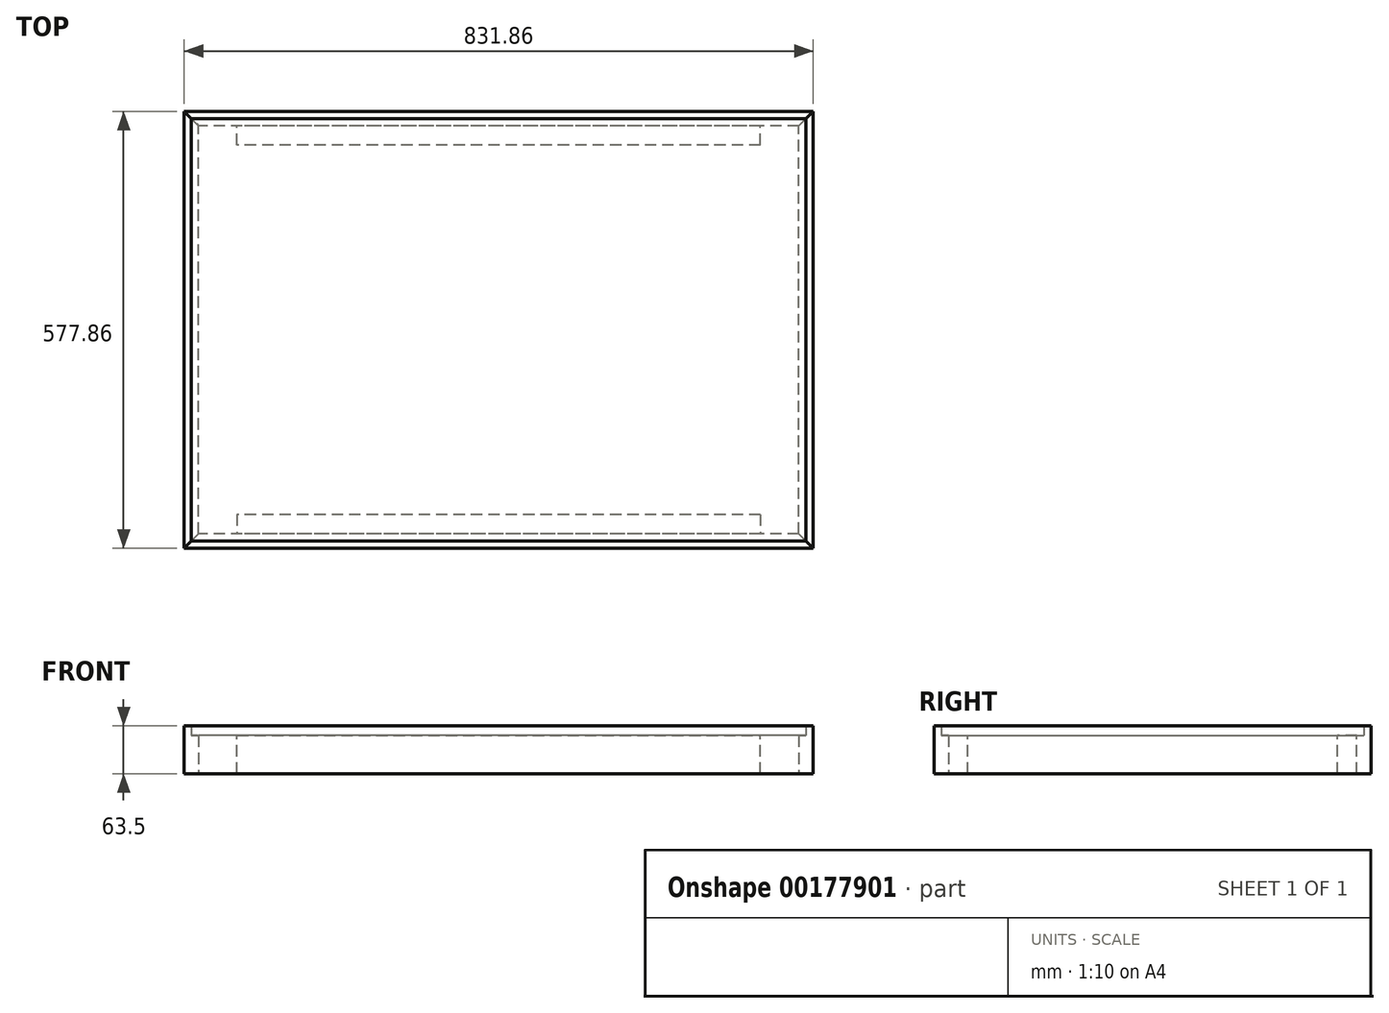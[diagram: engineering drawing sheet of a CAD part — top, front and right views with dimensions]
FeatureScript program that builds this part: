
annotation { "Feature Type Name" : "Feature", "Feature Type Description" : "" }
export const myFeature = defineFeature(function(context is Context, id is Id, definition is map)
    precondition{}
    {
        {
            var Q0;
            Q0=qCreatedBy(makeId("Top.planeOp"),FACE);
            var sketch = newSketch(context, id + "F0", { "sketchPlane" : qUnion([Q0])});
            skLineSegment(sketch, "E0.bottom", {"start": v(406.4, -279.4) * mm, "end": v(-406.4, -279.4) * mm});
            skLineSegment(sketch, "E0.top", {"start": v(406.4, 279.4) * mm, "end": v(-406.4, 279.4) * mm});
            skLineSegment(sketch, "E0.left", {"start": v(406.4, -279.4) * mm, "end": v(406.4, 279.4) * mm});
            skLineSegment(sketch, "E0.right", {"start": v(-406.4, -279.4) * mm, "end": v(-406.4, 279.4) * mm});
            skPoint(sketch, "E0.middle", {"position": v(0, 0) * mm});
            skLineSegment(sketch, "E1.0", {"start": v(-396.88, -269.87) * mm, "end": v(-396.88, 269.88) * mm});
            skLineSegment(sketch, "E1.1", {"start": v(396.88, -269.87) * mm, "end": v(-396.88, -269.87) * mm});
            skLineSegment(sketch, "E1.2", {"start": v(396.88, -269.87) * mm, "end": v(396.88, 269.88) * mm});
            skLineSegment(sketch, "E1.3", {"start": v(396.88, 269.88) * mm, "end": v(-396.88, 269.88) * mm});
            skLineSegment(sketch, "E2.0", {"start": v(-415.93, -288.92) * mm, "end": v(-415.93, 288.93) * mm});
            skLineSegment(sketch, "E2.1", {"start": v(415.93, -288.92) * mm, "end": v(-415.93, -288.92) * mm});
            skLineSegment(sketch, "E2.2", {"start": v(415.93, -288.92) * mm, "end": v(415.93, 288.93) * mm});
            skLineSegment(sketch, "E2.3", {"start": v(415.93, 288.93) * mm, "end": v(-415.93, 288.93) * mm});
            skLineSegment(sketch, "E3", {"start": v(-415.93, 288.93) * mm, "end": v(-396.88, 269.88) * mm});
            skLineSegment(sketch, "E4", {"start": v(-415.93, -288.92) * mm, "end": v(-396.88, -269.87) * mm});
            skLineSegment(sketch, "E5", {"start": v(396.88, -269.87) * mm, "end": v(415.93, -288.92) * mm});
            skLineSegment(sketch, "E6", {"start": v(396.88, 269.88) * mm, "end": v(415.93, 288.93) * mm});
            skSolve(sketch);
        }
        {
            var Q0;
            Q0=makeQuery(id+"F0.imprint","IMPRINT",FACE,{"disambiguationData":[TD([[makeQuery(id+"F0.imprint","IMPRINT",EDGE,{"derivedFrom":sQuery(id+"F0.wireOp",EDGE,"E0.bottom")}),-1.0]])]});
            var Q1;
            Q1=makeQuery(id+"F0.imprint","IMPRINT",FACE,{"disambiguationData":[TD([[makeQuery(id+"F0.imprint","IMPRINT",EDGE,{"derivedFrom":sQuery(id+"F0.wireOp",EDGE,"E1.0")}),-1.0]])]});
            var Q2;
            {var subQ0=sQuery(id+"F0.wireOp",EDGE,"E0.right");Q2=makeQuery(id+"F0.imprint","IMPRINT",FACE,{"disambiguationData":[TD([[makeQuery(id+"F0.imprint","IMPRINT",EDGE,{"derivedFrom":subQ0}),-1.0]])]});}
            var Q3;
            {var subQ0=sQuery(id+"F0.wireOp",EDGE,"E0.top");Q3=makeQuery(id+"F0.imprint","IMPRINT",FACE,{"disambiguationData":[TD([[makeQuery(id+"F0.imprint","IMPRINT",EDGE,{"derivedFrom":subQ0}),1.0]])]});}
            var Q4;
            {var subQ0=sQuery(id+"F0.wireOp",EDGE,"E0.left");Q4=makeQuery(id+"F0.imprint","IMPRINT",FACE,{"disambiguationData":[TD([[makeQuery(id+"F0.imprint","IMPRINT",EDGE,{"derivedFrom":subQ0}),1.0]])]});}
            extrude(context, id + "F1", {"entities" : qUnion([Q0, Q1, Q2, Q3, Q4]), "depth" : 12.7 * mm});
        }
        {
            var Q0;
            {var subQ0=sQuery(id+"F0.wireOp",EDGE,"E0.right");Q0=makeQuery(id+"F0.imprint","IMPRINT",FACE,{"disambiguationData":[TD([[makeQuery(id+"F0.imprint","IMPRINT",EDGE,{"derivedFrom":subQ0}),-1.0]])]});}
            var Q1;
            {var subQ0=sQuery(id+"F0.wireOp",EDGE,"E0.right");Q1=makeQuery(id+"F0.imprint","IMPRINT",FACE,{"disambiguationData":[TD([[makeQuery(id+"F0.imprint","IMPRINT",EDGE,{"derivedFrom":subQ0}),1.0]])]});}
            var Q2;
            Q2=makeQuery(id+"F1.opExtrude","CAP_FACE",FACE,{"disambiguationData":[OSD([sQuery(id+"F0.wireOp",EDGE,"E0.bottom"),sQuery(id+"F0.wireOp",EDGE,"E0.top"),sQuery(id+"F0.wireOp",EDGE,"E0.left"),sQuery(id+"F0.wireOp",EDGE,"E0.right")])],"isStart":false});
            extrude(context, id + "F2", {"entities" : qUnion([Q0, Q1]), "endBound" : BoundingType.UP_TO_SURFACE, "endBoundEntityFace" : qUnion([Q2]), "depth" : 25.4 * mm, "hasSecondDirection" : true, "secondDirectionOppositeDirection" : true, "secondDirectionDepth" : 50.8 * mm});
        }
        {
            var Q0;
            {var subQ0=sQuery(id+"F0.wireOp",EDGE,"E0.bottom");Q0=makeQuery(id+"F0.imprint","IMPRINT",FACE,{"disambiguationData":[TD([[makeQuery(id+"F0.imprint","IMPRINT",EDGE,{"derivedFrom":subQ0}),-1.0]])]});}
            var Q1;
            {var subQ0=sQuery(id+"F0.wireOp",EDGE,"E0.bottom");Q1=makeQuery(id+"F0.imprint","IMPRINT",FACE,{"disambiguationData":[TD([[makeQuery(id+"F0.imprint","IMPRINT",EDGE,{"derivedFrom":subQ0}),1.0]])]});}
            var Q2;
            Q2=makeQuery(id+"F1.opExtrude","CAP_FACE",FACE,{"disambiguationData":[OSD([sQuery(id+"F0.wireOp",EDGE,"E0.bottom"),sQuery(id+"F0.wireOp",EDGE,"E0.top"),sQuery(id+"F0.wireOp",EDGE,"E0.left"),sQuery(id+"F0.wireOp",EDGE,"E0.right")])],"isStart":false});
            var Q3;
            Q3=makeQuery(id+"F2.opExtrude","CAP_FACE",FACE,{"disambiguationData":[OSD([sQuery(id+"F0.wireOp",EDGE,"E1.0"),sQuery(id+"F0.wireOp",EDGE,"E2.0"),sQuery(id+"F0.wireOp",EDGE,"E3"),sQuery(id+"F0.wireOp",EDGE,"E4")])],"isStart":true});
            extrude(context, id + "F3", {"entities" : qUnion([Q0, Q1]), "endBound" : BoundingType.UP_TO_SURFACE, "endBoundEntityFace" : qUnion([Q2]), "depth" : 25.4 * mm, "hasSecondDirection" : true, "secondDirectionBound" : SecondDirectionBoundingType.UP_TO_SURFACE, "secondDirectionOppositeDirection" : true, "secondDirectionBoundEntityFace" : qUnion([Q3]), "secondDirectionDepth" : 25.4 * mm});
        }
        {
            var Q0;
            {var subQ0=sQuery(id+"F0.wireOp",EDGE,"E0.left");Q0=makeQuery(id+"F0.imprint","IMPRINT",FACE,{"disambiguationData":[TD([[makeQuery(id+"F0.imprint","IMPRINT",EDGE,{"derivedFrom":subQ0}),1.0]])]});}
            var Q1;
            {var subQ0=sQuery(id+"F0.wireOp",EDGE,"E0.left");Q1=makeQuery(id+"F0.imprint","IMPRINT",FACE,{"disambiguationData":[TD([[makeQuery(id+"F0.imprint","IMPRINT",EDGE,{"derivedFrom":subQ0}),-1.0]])]});}
            var Q2;
            Q2=makeQuery(id+"F1.opExtrude","CAP_FACE",FACE,{"disambiguationData":[OSD([sQuery(id+"F0.wireOp",EDGE,"E0.bottom"),sQuery(id+"F0.wireOp",EDGE,"E0.top"),sQuery(id+"F0.wireOp",EDGE,"E0.left"),sQuery(id+"F0.wireOp",EDGE,"E0.right")])],"isStart":false});
            var Q3;
            Q3=makeQuery(id+"F2.opExtrude","CAP_FACE",FACE,{"disambiguationData":[OSD([sQuery(id+"F0.wireOp",EDGE,"E1.0"),sQuery(id+"F0.wireOp",EDGE,"E2.0"),sQuery(id+"F0.wireOp",EDGE,"E3"),sQuery(id+"F0.wireOp",EDGE,"E4")])],"isStart":true});
            extrude(context, id + "F4", {"entities" : qUnion([Q0, Q1]), "endBound" : BoundingType.UP_TO_SURFACE, "endBoundEntityFace" : qUnion([Q2]), "depth" : 25.4 * mm, "hasSecondDirection" : true, "secondDirectionBound" : SecondDirectionBoundingType.UP_TO_SURFACE, "secondDirectionOppositeDirection" : true, "secondDirectionBoundEntityFace" : qUnion([Q3]), "secondDirectionDepth" : 25.4 * mm});
        }
        {
            var Q0;
            {var subQ0=sQuery(id+"F0.wireOp",EDGE,"E0.top");Q0=makeQuery(id+"F0.imprint","IMPRINT",FACE,{"disambiguationData":[TD([[makeQuery(id+"F0.imprint","IMPRINT",EDGE,{"derivedFrom":subQ0}),1.0]])]});}
            var Q1;
            {var subQ0=sQuery(id+"F0.wireOp",EDGE,"E0.top");Q1=makeQuery(id+"F0.imprint","IMPRINT",FACE,{"disambiguationData":[TD([[makeQuery(id+"F0.imprint","IMPRINT",EDGE,{"derivedFrom":subQ0}),-1.0]])]});}
            var Q2;
            Q2=makeQuery(id+"F1.opExtrude","CAP_FACE",FACE,{"disambiguationData":[OSD([sQuery(id+"F0.wireOp",EDGE,"E0.bottom"),sQuery(id+"F0.wireOp",EDGE,"E0.top"),sQuery(id+"F0.wireOp",EDGE,"E0.left"),sQuery(id+"F0.wireOp",EDGE,"E0.right")])],"isStart":false});
            var Q3;
            Q3=makeQuery(id+"F2.opExtrude","CAP_FACE",FACE,{"disambiguationData":[OSD([sQuery(id+"F0.wireOp",EDGE,"E1.0"),sQuery(id+"F0.wireOp",EDGE,"E2.0"),sQuery(id+"F0.wireOp",EDGE,"E3"),sQuery(id+"F0.wireOp",EDGE,"E4")])],"isStart":true});
            extrude(context, id + "F5", {"entities" : qUnion([Q0, Q1]), "endBound" : BoundingType.UP_TO_SURFACE, "endBoundEntityFace" : qUnion([Q2]), "depth" : 25.4 * mm, "hasSecondDirection" : true, "secondDirectionBound" : SecondDirectionBoundingType.UP_TO_SURFACE, "secondDirectionOppositeDirection" : true, "secondDirectionBoundEntityFace" : qUnion([Q3]), "secondDirectionDepth" : 25.4 * mm});
        }
        {
            var Q0;
            Q0=makeQuery(id+"F1.opExtrude","SWEPT_BODY",BODY,{"disambiguationData":[OSD([sQuery(id+"F0.wireOp",EDGE,"E0.bottom"),sQuery(id+"F0.wireOp",EDGE,"E0.top"),sQuery(id+"F0.wireOp",EDGE,"E0.left"),sQuery(id+"F0.wireOp",EDGE,"E0.right")])]});
            var Q1;
            Q1=makeQuery(id+"F2.opExtrude","SWEPT_BODY",BODY,{"disambiguationData":[OSD([sQuery(id+"F0.wireOp",EDGE,"E1.0"),sQuery(id+"F0.wireOp",EDGE,"E2.0"),sQuery(id+"F0.wireOp",EDGE,"E3"),sQuery(id+"F0.wireOp",EDGE,"E4")])]});
            var Q2;
            Q2=makeQuery(id+"F3.opExtrude","SWEPT_BODY",BODY,{"disambiguationData":[OSD([sQuery(id+"F0.wireOp",EDGE,"E1.1"),sQuery(id+"F0.wireOp",EDGE,"E2.1"),sQuery(id+"F0.wireOp",EDGE,"E4"),sQuery(id+"F0.wireOp",EDGE,"E5")])]});
            var Q3;
            Q3=makeQuery(id+"F4.opExtrude","SWEPT_BODY",BODY,{"disambiguationData":[OSD([sQuery(id+"F0.wireOp",EDGE,"E1.2"),sQuery(id+"F0.wireOp",EDGE,"E2.2"),sQuery(id+"F0.wireOp",EDGE,"E5"),sQuery(id+"F0.wireOp",EDGE,"E6")])]});
            var Q4;
            Q4=makeQuery(id+"F5.opExtrude","SWEPT_BODY",BODY,{"disambiguationData":[OSD([sQuery(id+"F0.wireOp",EDGE,"E1.3"),sQuery(id+"F0.wireOp",EDGE,"E2.3"),sQuery(id+"F0.wireOp",EDGE,"E3"),sQuery(id+"F0.wireOp",EDGE,"E6")])]});
            booleanBodies(context, id + "F6", {"operationType" : BooleanOperationType.SUBTRACTION, "tools" : qUnion([Q0]), "targets" : qUnion([Q1, Q2, Q3, Q4]), "keepTools" : true});
        }
        {
            var Q0;
            Q0=makeQuery(id+"F1.opExtrude","CAP_FACE",FACE,{"disambiguationData":[OSD([sQuery(id+"F0.wireOp",EDGE,"E0.bottom"),sQuery(id+"F0.wireOp",EDGE,"E0.top"),sQuery(id+"F0.wireOp",EDGE,"E0.left"),sQuery(id+"F0.wireOp",EDGE,"E0.right")])],"isStart":true});
            var sketch = newSketch(context, id + "F7", { "sketchPlane" : qUnion([Q0])});
            skLineSegment(sketch, "E7.0", {"start": v(396.88, 269.87) * mm, "end": v(-396.88, 269.88) * mm, "construction": true});
            skLineSegment(sketch, "E8.0", {"start": v(-396.88, 269.88) * mm, "end": v(-396.88, -269.88) * mm, "construction": true});
            skLineSegment(sketch, "E9.0", {"start": v(396.88, 269.87) * mm, "end": v(396.88, -269.88) * mm, "construction": true});
            skLineSegment(sketch, "E10.bottom", {"start": v(-346.07, 269.87) * mm, "end": v(346.08, 269.87) * mm});
            skLineSegment(sketch, "E10.top", {"start": v(-346.07, 244.47) * mm, "end": v(346.08, 244.47) * mm});
            skLineSegment(sketch, "E10.left", {"start": v(-346.07, 269.87) * mm, "end": v(-346.07, 244.47) * mm});
            skLineSegment(sketch, "E10.right", {"start": v(346.08, 269.87) * mm, "end": v(346.08, 244.47) * mm});
            skLineSegment(sketch, "E11", {"start": v(-396.88, 0) * mm, "end": v(396.88, 0) * mm, "construction": true});
            skLineSegment(sketch, "E12.MirrorCS", {"start": v(-346.08, -269.88) * mm, "end": v(346.08, -269.88) * mm});
            skLineSegment(sketch, "E13.MirrorCS", {"start": v(-346.08, -244.48) * mm, "end": v(346.08, -244.48) * mm});
            skLineSegment(sketch, "E14.MirrorCS", {"start": v(-346.08, -269.88) * mm, "end": v(-346.08, -244.48) * mm});
            skLineSegment(sketch, "E15.MirrorCS", {"start": v(346.08, -269.88) * mm, "end": v(346.08, -244.48) * mm});
            skSolve(sketch);
        }
        {
            var Q0;
            Q0=makeQuery(id+"F7.imprint","IMPRINT",FACE,{"disambiguationData":[TD([[makeQuery(id+"F7.imprint","IMPRINT",EDGE,{"derivedFrom":sQuery(id+"F7.wireOp",EDGE,"E10.bottom")}),-1.0]])]});
            var Q1;
            Q1=makeQuery(id+"F7.imprint","IMPRINT",FACE,{"disambiguationData":[TD([[makeQuery(id+"F7.imprint","IMPRINT",EDGE,{"derivedFrom":sQuery(id+"F7.wireOp",EDGE,"E12.MirrorCS")}),1.0]])]});
            var Q2;
            Q2=makeQuery(id+"F2.opExtrude","CAP_FACE",FACE,{"disambiguationData":[OSD([sQuery(id+"F0.wireOp",EDGE,"E1.0"),sQuery(id+"F0.wireOp",EDGE,"E2.0"),sQuery(id+"F0.wireOp",EDGE,"E3"),sQuery(id+"F0.wireOp",EDGE,"E4")])],"isStart":true});
            extrude(context, id + "F8", {"entities" : qUnion([Q0, Q1]), "endBound" : BoundingType.UP_TO_SURFACE, "endBoundEntityFace" : qUnion([Q2]), "depth" : 25.4 * mm});
        }
    });
